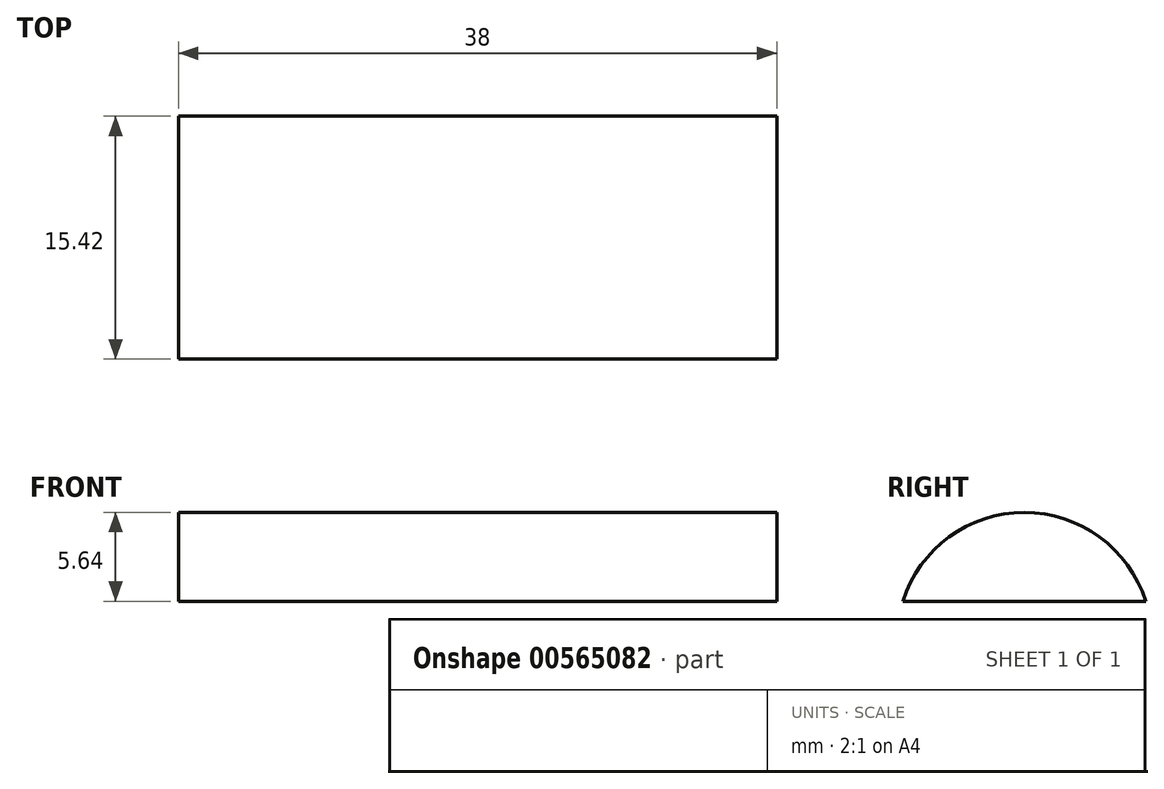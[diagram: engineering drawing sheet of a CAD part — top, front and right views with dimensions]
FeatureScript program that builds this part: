
annotation { "Feature Type Name" : "Feature", "Feature Type Description" : "" }
export const myFeature = defineFeature(function(context is Context, id is Id, definition is map)
    precondition{}
    {
        {
            var Q0;
            Q0=qCreatedBy(makeId("Right.planeOp"),FACE);
            var sketch = newSketch(context, id + "F0", { "sketchPlane" : qUnion([Q0])});
            skLineSegment(sketch, "E0", {"start": v(-19.46, 0) * mm, "end": v(6.54, 0) * mm, "construction": true});
            skLineSegment(sketch, "E1", {"start": v(6.54, 0) * mm, "end": v(6.54, 9) * mm, "construction": true});
            skLineSegment(sketch, "E2", {"start": v(6.54, 9) * mm, "end": v(-19.46, 0) * mm, "construction": true});
            skArc(sketch, "E3", {"start": v(8.42, 0) * mm, "mid": v(0.71, 5.64) * mm, "end": v(-7, 0) * mm});
            skPoint(sketch, "E3.first.point", {"position": v(-7.25, 0) * mm});
            skPoint(sketch, "E3.second.point", {"position": v(-0.57, 6.54) * mm});
            skPoint(sketch, "E3.third.point", {"position": v(8.67, 0) * mm});
            skLineSegment(sketch, "E4", {"start": v(-7, 0) * mm, "end": v(8.42, 0) * mm});
            skSolve(sketch);
        }
        {
            var Q0;
            Q0=makeQuery(id+"F0.imprint","IMPRINT",FACE,{"disambiguationData":[TD([[makeQuery(id+"F0.imprint","IMPRINT",EDGE,{"derivedFrom":sQuery(id+"F0.wireOp",EDGE,"E3")}),1.0]])]});
            extrude(context, id + "F1", {"entities" : qUnion([Q0]), "depth" : 38 * mm, "offsetDistance" : 25 * mm});
        }
    });
